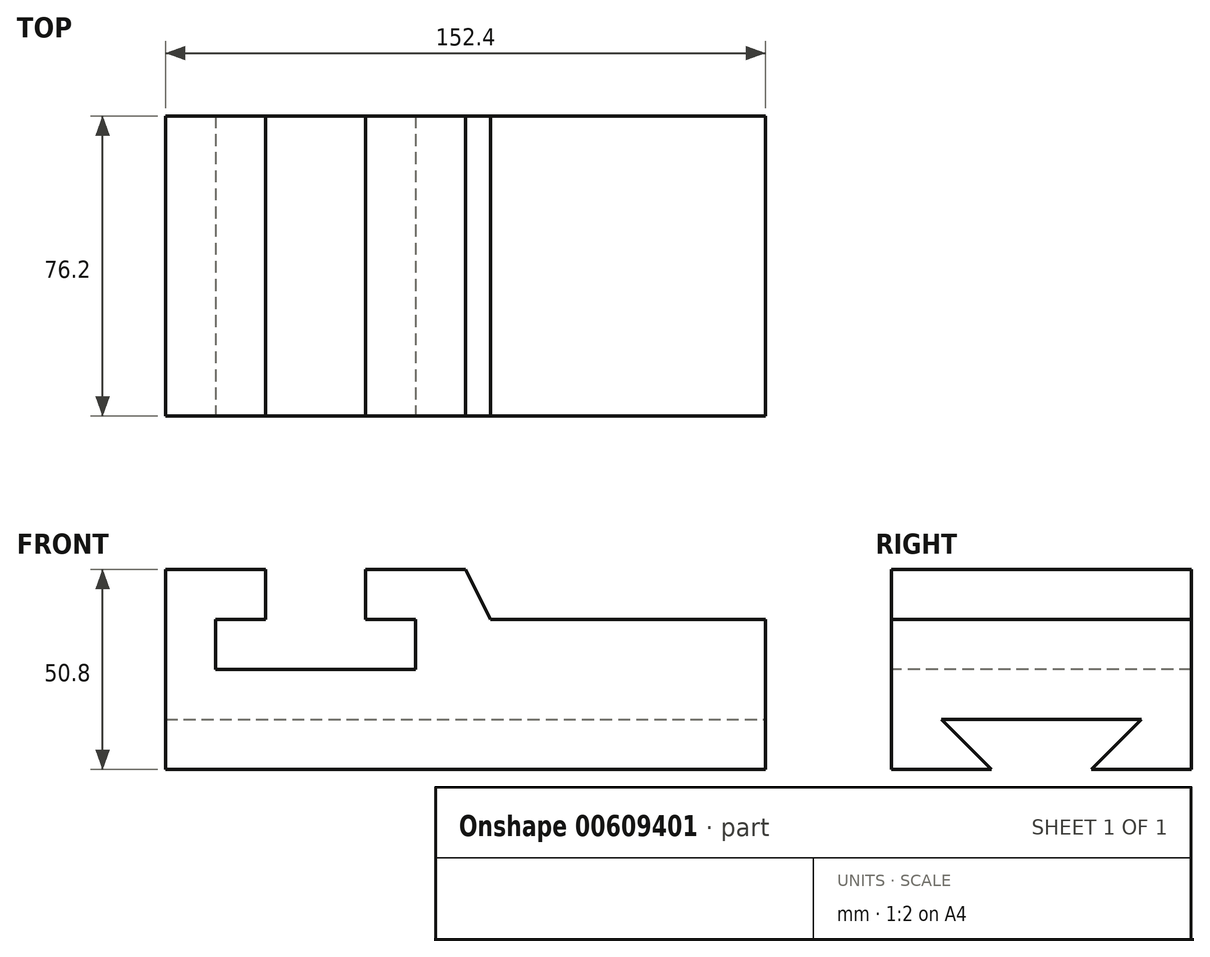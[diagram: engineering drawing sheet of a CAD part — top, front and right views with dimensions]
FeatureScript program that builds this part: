
annotation { "Feature Type Name" : "Feature", "Feature Type Description" : "" }
export const myFeature = defineFeature(function(context is Context, id is Id, definition is map)
    precondition{}
    {
        {
            var Q0;
            Q0=qCreatedBy(makeId("Front.planeOp"),FACE);
            var sketch = newSketch(context, id + "F0", { "sketchPlane" : qUnion([Q0])});
            skLineSegment(sketch, "E0", {"start": v(0, 0) * mm, "end": v(152.4, 0) * mm});
            skLineSegment(sketch, "E1", {"start": v(152.4, 0) * mm, "end": v(152.4, 50.8) * mm});
            skLineSegment(sketch, "E2", {"start": v(152.4, 50.8) * mm, "end": v(0, 50.8) * mm});
            skLineSegment(sketch, "E3", {"start": v(0, 50.8) * mm, "end": v(0, 0) * mm});
            skSolve(sketch);
        }
        {
            var Q0;
            Q0 = qSketchRegion(id + "F0", true);
            extrude(context, id + "F1", {"entities" : qUnion([Q0]), "depth" : 76.2 * mm, "offsetDistance" : 25.4 * mm});
        }
        {
            var Q0;
            Q0=makeQuery(id+"F1.opExtrude","CAP_FACE",FACE,{"disambiguationData":[OSD([sQuery(id+"F0.wireOp",EDGE,"E0"),sQuery(id+"F0.wireOp",EDGE,"E1"),sQuery(id+"F0.wireOp",EDGE,"E2"),sQuery(id+"F0.wireOp",EDGE,"E3")])],"isStart":false});
            var sketch = newSketch(context, id + "F2", { "sketchPlane" : qUnion([Q0])});
            skLineSegment(sketch, "E4", {"start": v(0, 50.8) * mm, "end": v(25.4, 50.8) * mm});
            skLineSegment(sketch, "E5", {"start": v(25.4, 50.8) * mm, "end": v(25.4, 38.1) * mm});
            skLineSegment(sketch, "E6", {"start": v(25.4, 38.1) * mm, "end": v(12.7, 38.1) * mm});
            skPoint(sketch, "E6.endSnap0", {"position": v(12.7, 50.8) * mm});
            skLineSegment(sketch, "E7", {"start": v(12.7, 38.1) * mm, "end": v(12.7, 25.4) * mm});
            skLineSegment(sketch, "E8", {"start": v(12.7, 25.4) * mm, "end": v(63.5, 25.4) * mm});
            skLineSegment(sketch, "E9", {"start": v(63.5, 25.4) * mm, "end": v(63.5, 38.1) * mm});
            skLineSegment(sketch, "E10", {"start": v(63.5, 38.1) * mm, "end": v(50.8, 38.1) * mm});
            skLineSegment(sketch, "E11", {"start": v(50.8, 38.1) * mm, "end": v(50.8, 50.8) * mm});
            skLineSegment(sketch, "E12", {"start": v(50.8, 50.8) * mm, "end": v(76.2, 50.8) * mm});
            skLineSegment(sketch, "E13", {"start": v(25.4, 50.8) * mm, "end": v(50.8, 50.8) * mm});
            skSolve(sketch);
        }
        {
            var Q0;
            Q0 = qSketchRegion(id + "F2", true);
            extrude(context, id + "F3", {"entities" : qUnion([Q0]), "operationType" : NewBodyOperationType.REMOVE, "oppositeDirection" : true, "depth" : 76.2 * mm, "offsetDistance" : 25.4 * mm});
        }
        {
            var Q0;
            Q0=makeQuery(id+"F1.opExtrude","CAP_FACE",FACE,{"disambiguationData":[OSD([sQuery(id+"F0.wireOp",EDGE,"E0"),sQuery(id+"F0.wireOp",EDGE,"E1"),sQuery(id+"F0.wireOp",EDGE,"E2"),sQuery(id+"F0.wireOp",EDGE,"E3")])],"isStart":false});
            var sketch = newSketch(context, id + "F4", { "sketchPlane" : qUnion([Q0])});
            skLineSegment(sketch, "E14", {"start": v(50.8, 50.8) * mm, "end": v(76.2, 50.8) * mm});
            skLineSegment(sketch, "E15", {"start": v(76.2, 50.8) * mm, "end": v(82.55, 50.8) * mm});
            skLineSegment(sketch, "E16", {"start": v(82.55, 50.8) * mm, "end": v(82.55, 38.1) * mm});
            skLineSegment(sketch, "E17", {"start": v(76.2, 50.8) * mm, "end": v(82.55, 38.1) * mm});
            skSolve(sketch);
        }
        {
            var Q0;
            Q0 = qSketchRegion(id + "F4", true);
            extrude(context, id + "F5", {"entities" : qUnion([Q0]), "operationType" : NewBodyOperationType.REMOVE, "oppositeDirection" : true, "depth" : 76.2 * mm, "offsetDistance" : 25.4 * mm});
        }
        {
            var Q0;
            Q0=makeQuery(id+"F1.opExtrude","CAP_FACE",FACE,{"disambiguationData":[OSD([sQuery(id+"F0.wireOp",EDGE,"E0"),sQuery(id+"F0.wireOp",EDGE,"E1"),sQuery(id+"F0.wireOp",EDGE,"E2"),sQuery(id+"F0.wireOp",EDGE,"E3")])],"isStart":false});
            var sketch = newSketch(context, id + "F6", { "sketchPlane" : qUnion([Q0])});
            skLineSegment(sketch, "E18", {"start": v(82.55, 38.1) * mm, "end": v(152.4, 38.1) * mm});
            skLineSegment(sketch, "E19", {"start": v(152.4, 38.1) * mm, "end": v(152.4, 50.8) * mm});
            skLineSegment(sketch, "E20", {"start": v(152.4, 50.8) * mm, "end": v(82.55, 50.8) * mm});
            skLineSegment(sketch, "E21", {"start": v(82.55, 50.8) * mm, "end": v(82.55, 38.1) * mm});
            skSolve(sketch);
        }
        {
            var Q0;
            Q0 = qSketchRegion(id + "F6", true);
            extrude(context, id + "F7", {"entities" : qUnion([Q0]), "operationType" : NewBodyOperationType.REMOVE, "oppositeDirection" : true, "depth" : 76.2 * mm, "offsetDistance" : 25.4 * mm});
        }
        {
            var Q0;
            Q0=makeQuery(id+"F1.opExtrude","SWEPT_FACE",FACE,{"disambiguationData":[OSD([sQuery(id+"F0.wireOp",EDGE,"E1")])]});
            var sketch = newSketch(context, id + "F8", { "sketchPlane" : qUnion([Q0])});
            skLineSegment(sketch, "E22", {"start": v(-76.2, 0) * mm, "end": v(-50.8, 0) * mm});
            skLineSegment(sketch, "E23", {"start": v(-50.8, 0) * mm, "end": v(-50.8, 12.7) * mm});
            skLineSegment(sketch, "E24", {"start": v(0, 0) * mm, "end": v(-25.4, 0) * mm});
            skLineSegment(sketch, "E25", {"start": v(-25.4, 0) * mm, "end": v(-25.4, 12.7) * mm});
            skLineSegment(sketch, "E26", {"start": v(-25.4, 12.7) * mm, "end": v(-12.7, 12.7) * mm});
            skPoint(sketch, "E26.endSnap0", {"position": v(-12.7, 0) * mm});
            skLineSegment(sketch, "E27", {"start": v(-50.8, 12.7) * mm, "end": v(-63.5, 12.7) * mm});
            skLineSegment(sketch, "E28", {"start": v(-63.5, 12.7) * mm, "end": v(-50.8, 0) * mm});
            skLineSegment(sketch, "E29", {"start": v(-12.7, 12.7) * mm, "end": v(-25.4, 0) * mm});
            skLineSegment(sketch, "E30", {"start": v(-63.5, 12.7) * mm, "end": v(-12.7, 12.7) * mm});
            skLineSegment(sketch, "E31", {"start": v(-25.4, 0) * mm, "end": v(-50.8, 0) * mm});
            skLineSegment(sketch, "E32", {"start": v(-50.8, 0) * mm, "end": v(-63.5, 12.7) * mm});
            skSolve(sketch);
        }
        {
            var Q0;
            {var subQ0=sQuery(id+"F8.wireOp",EDGE,"E23");Q0=makeQuery(id+"F8.imprint","IMPRINT",FACE,{"disambiguationData":[TD([[makeQuery(id+"F8.imprint","IMPRINT",EDGE,{"derivedFrom":subQ0}),1.0]])]});}
            var Q1;
            {var subQ0=sQuery(id+"F8.wireOp",EDGE,"E23");Q1=makeQuery(id+"F8.imprint","IMPRINT",FACE,{"disambiguationData":[TD([[makeQuery(id+"F8.imprint","IMPRINT",EDGE,{"derivedFrom":subQ0}),-1.0]])]});}
            var Q2;
            {var subQ0=sQuery(id+"F8.wireOp",EDGE,"E25");Q2=makeQuery(id+"F8.imprint","IMPRINT",FACE,{"disambiguationData":[TD([[makeQuery(id+"F8.imprint","IMPRINT",EDGE,{"derivedFrom":subQ0}),-1.0]])]});}
            extrude(context, id + "F9", {"entities" : qUnion([Q0, Q1, Q2]), "operationType" : NewBodyOperationType.REMOVE, "oppositeDirection" : true, "depth" : 152.4 * mm, "offsetDistance" : 25.4 * mm});
        }
    });
